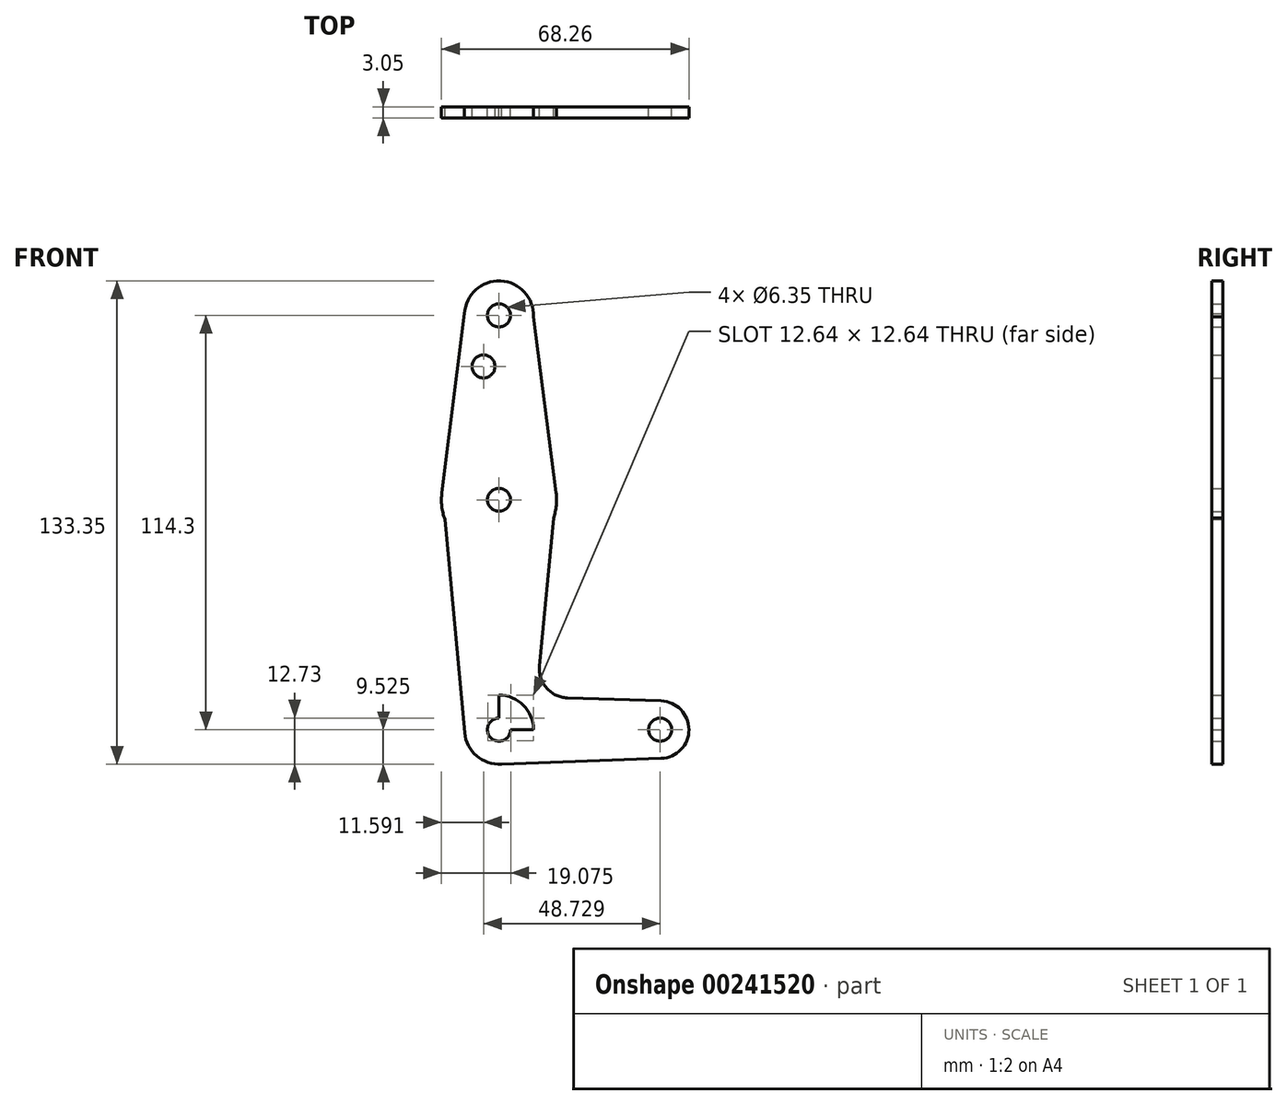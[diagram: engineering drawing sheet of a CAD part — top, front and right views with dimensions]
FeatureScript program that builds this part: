
annotation { "Feature Type Name" : "Feature", "Feature Type Description" : "" }
export const myFeature = defineFeature(function(context is Context, id is Id, definition is map)
    precondition{}
    {
        {
            var Q0;
            Q0=qCreatedBy(makeId("Front.planeOp"),FACE);
            var sketch = newSketch(context, id + "F0", { "sketchPlane" : qUnion([Q0])});
            skLineSegment(sketch, "E0", {"start": v(0, 59.86) * mm, "end": v(0, -54.44) * mm});
            skCircle(sketch, "E1", {"center": v(0, -54.44) * mm, "radius": 9.53 * mm});
            skCircle(sketch, "E2", {"center": v(0, 59.86) * mm, "radius": 9.53 * mm});
            skLineSegment(sketch, "E3", {"start": v(0, -54.44) * mm, "end": v(44.45, -54.44) * mm});
            skCircle(sketch, "E4", {"center": v(44.45, -54.44) * mm, "radius": 7.94 * mm});
            skCircle(sketch, "E5", {"center": v(0, 8.99) * mm, "radius": 15.88 * mm});
            skLineSegment(sketch, "E6", {"start": v(-9.51, 60.33) * mm, "end": v(-16.29, 6.7) * mm});
            skLineSegment(sketch, "E7", {"start": v(9.52, 59.48) * mm, "end": v(16.3, 6.7) * mm});
            skLineSegment(sketch, "E8", {"start": v(-14.9, 3.53) * mm, "end": v(-9.48, -55.3) * mm});
            skLineSegment(sketch, "E9", {"start": v(44.7, -46.5) * mm, "end": v(18.84, -45.67) * mm});
            skLineSegment(sketch, "E10", {"start": v(15.06, 3.96) * mm, "end": v(11.18, -36.97) * mm});
            skPoint(sketch, "E11.visualSharp", {"position": v(10.38, -45.4) * mm});
            skArc(sketch, "E11.filletArc", {"start": v(11.18, -36.97) * mm, "mid": v(13.13, -42.98) * mm, "end": v(18.84, -45.67) * mm});
            skCircle(sketch, "E12", {"center": v(-4.28, 45.78) * mm, "radius": 1.59 * mm});
            skCircle(sketch, "E13", {"center": v(0, 59.86) * mm, "radius": 3.18 * mm});
            skCircle(sketch, "E14", {"center": v(0, 8.99) * mm, "radius": 3.18 * mm});
            skCircle(sketch, "E15", {"center": v(0, -54.44) * mm, "radius": 3.18 * mm});
            skCircle(sketch, "E16", {"center": v(44.45, -54.44) * mm, "radius": 3.18 * mm});
            skLineSegment(sketch, "E17", {"start": v(0, -63.96) * mm, "end": v(44.73, -62.37) * mm});
            skCircle(sketch, "E18", {"center": v(-4.28, 45.78) * mm, "radius": 3.18 * mm});
            skSolve(sketch);
        }
        {
            var Q0;
            Q0 = qSketchRegion(id + "F0", true);
            extrude(context, id + "F1", {"entities" : qUnion([Q0]), "depth" : 3.05 * mm});
        }
    });
